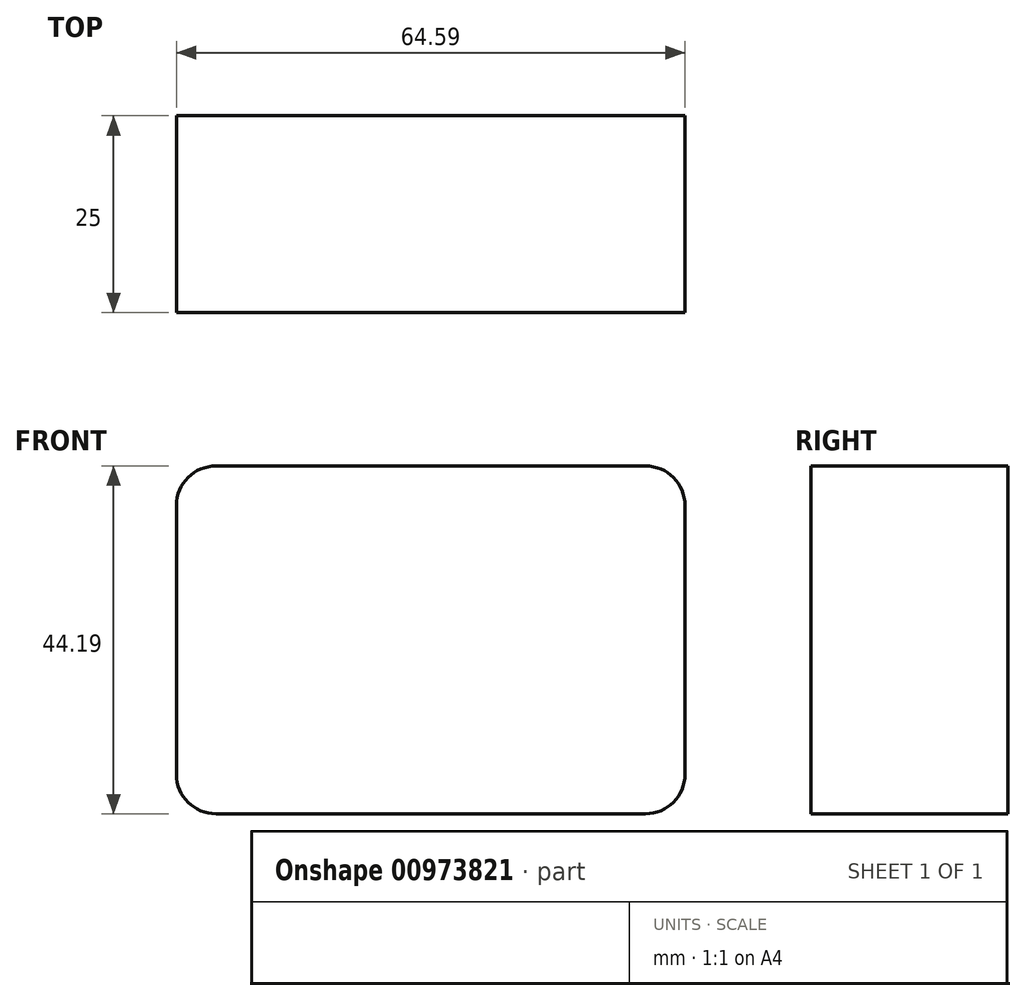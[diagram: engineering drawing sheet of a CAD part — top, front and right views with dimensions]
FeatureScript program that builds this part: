
annotation { "Feature Type Name" : "Feature", "Feature Type Description" : "" }
export const myFeature = defineFeature(function(context is Context, id is Id, definition is map)
    precondition{}
    {
        {
            var Q0;
            Q0=qCreatedBy(makeId("Front.planeOp"),FACE);
            var sketch = newSketch(context, id + "F0", { "sketchPlane" : qUnion([Q0])});
            skLineSegment(sketch, "E0.bottom", {"start": v(-100.94, 32.69) * mm, "end": v(-46.35, 32.69) * mm});
            skLineSegment(sketch, "E0.top", {"start": v(-100.94, -11.5) * mm, "end": v(-46.35, -11.5) * mm});
            skLineSegment(sketch, "E0.left", {"start": v(-105.94, 27.69) * mm, "end": v(-105.94, -6.5) * mm});
            skLineSegment(sketch, "E0.right", {"start": v(-41.35, 27.69) * mm, "end": v(-41.35, -6.5) * mm});
            skPoint(sketch, "E1.visualSharp", {"position": v(-105.94, 32.69) * mm});
            skArc(sketch, "E1.filletArc", {"start": v(-100.94, 32.69) * mm, "mid": v(-104.47, 31.22) * mm, "end": v(-105.94, 27.69) * mm});
            skPoint(sketch, "E2.visualSharp", {"position": v(-41.35, 32.69) * mm});
            skArc(sketch, "E2.filletArc", {"start": v(-41.35, 27.69) * mm, "mid": v(-42.82, 31.22) * mm, "end": v(-46.35, 32.69) * mm});
            skPoint(sketch, "E3.visualSharp", {"position": v(-41.35, -11.5) * mm});
            skArc(sketch, "E3.filletArc", {"start": v(-46.35, -11.5) * mm, "mid": v(-42.82, -10.03) * mm, "end": v(-41.35, -6.5) * mm});
            skPoint(sketch, "E4.visualSharp", {"position": v(-105.94, -11.5) * mm});
            skArc(sketch, "E4.filletArc", {"start": v(-105.94, -6.5) * mm, "mid": v(-104.47, -10.03) * mm, "end": v(-100.94, -11.5) * mm});
            skSolve(sketch);
        }
        {
            var Q0;
            Q0=makeQuery(id+"F0.imprint","IMPRINT",FACE,{"disambiguationData":[TD([[makeQuery(id+"F0.imprint","IMPRINT",EDGE,{"derivedFrom":sQuery(id+"F0.wireOp",EDGE,"E0.bottom")}),-1.0]])]});
            extrude(context, id + "F1", {"entities" : qUnion([Q0]), "depth" : 25 * mm, "offsetDistance" : 25 * mm});
        }
    });
